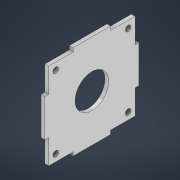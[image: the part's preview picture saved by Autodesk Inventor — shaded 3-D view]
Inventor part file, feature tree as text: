
AUTODESK INVENTOR PART (.ipt)
format: ipt  version: 2022 (Build 260153000, 153)  size: 191,488 bytes
history: native  units: in
note: dims shown in document units (in); Inventor stores cm internally (conversion verified against a paired STEP export)
features: sketch x8, extrude x4, hole x4
ambient origin geometry x8: Origin, YZ Plane, XZ Plane, XY Plane, X Axis, Y Axis, Z Axis, Center Point
bodies: Solid1 (feature_tree)
feature tree (16):
  extrude  "Extrusion1"  Depth=1.9685in
  hole  "Hole1"  [1 undecoded]
  hole  "Hole2"  [1 undecoded]
  hole  "Hole3"  [1 undecoded]
  hole  "Hole4"  [1 undecoded]
  extrude  "Extrusion3"  Depth=0.0787in
  extrude  "Extrusion4"  Depth=0.0787in
  extrude  "Extrusion5"  Depth=0.0787in
  sketch  "Sketch1"  dims[d0=1.9685in d1=1.9685in]
  sketch  "Sketch3"  dims[d2=1.8898in d3=1.8898in]
  sketch  "Sketch4"  dims[d4=0.0787in d5=0.0in d6=1.5197in]
  sketch  "Sketch5"  dims[d7=1.5197in d8=0.1181in]
  sketch  "Sketch6"  dims[d9=0.1225in d10=0.1225in]
  sketch  "Sketch7"  dims[d11=0.1225in]
  sketch  "Sketch8"  dims[d12=0.1181in d13=0.2362in d14=0.1575in d15=0.0787in d16=90.0deg d17=0.315in d18=0.8108in d19=1.5197in]
  sketch  "Sketch9"  dims[d20=1.5197in d21=0.1181in d22=0.1181in d23=0.2362in d24=0.1575in d25=0.0787in d26=90.0deg d27=0.315in d28=0.8108in d29=1.5197in d30=1.5197in d31=0.1181in d32=0.1181in d33=0.2362in d34=0.1575in d35=0.0787in d36=90.0deg d37=0.315in d38=0.8108in d39=1.5197in d40=1.5197in d41=0.1181in d42=0.1181in d43=0.2362in d44=0.1575in d45=0.0787in d46=90.0deg d47=0.315in d48=0.8108in d49=1.811in d50=1.811in d51=0.7874in d52=0.7874in d53=0.7874in d54=0.7874in d57=0.0787in d58=0.0in d59=0.7087in d60=0.0787in d61=0.0in d62=1.0827in d63=1.0827in d64=0.0787in d65=0.0787in d66=0.0787in d67=0.0787in d68=0.0787in d69=0.0in d55=0.5635in d56=0.0295in]
note: 4 required parameter values undecoded (feature->parameter linkage not recoverable at this tier; creation-order binding heuristic only, values carry confidence <= 0.55)
